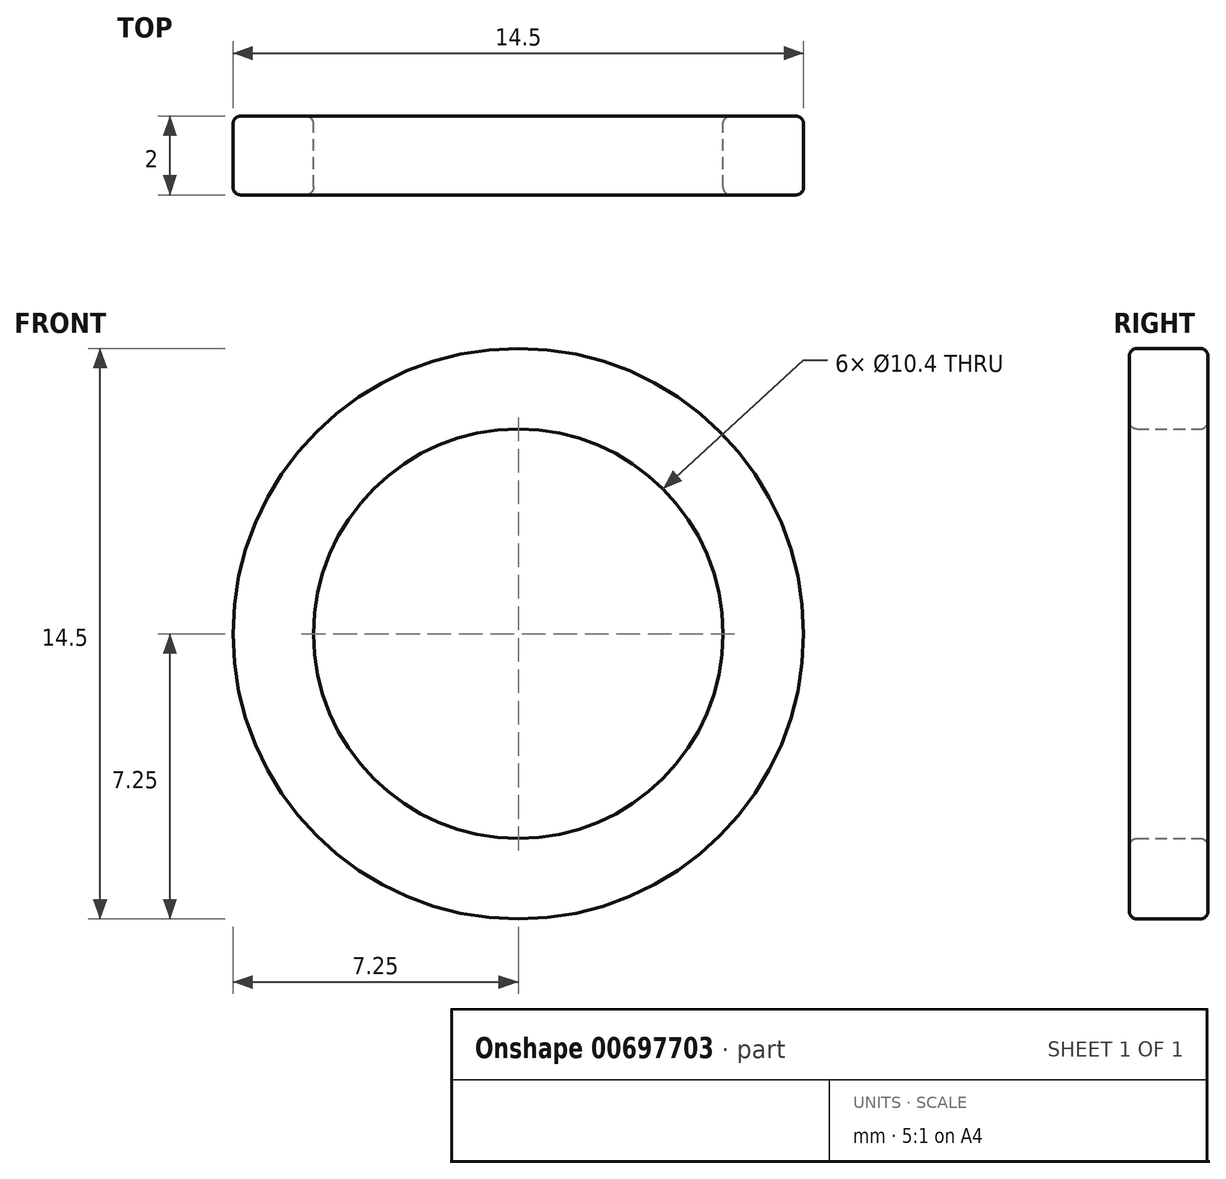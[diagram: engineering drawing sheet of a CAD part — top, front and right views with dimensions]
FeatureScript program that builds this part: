
annotation { "Feature Type Name" : "Feature", "Feature Type Description" : "" }
export const myFeature = defineFeature(function(context is Context, id is Id, definition is map)
    precondition{}
    {
        {
            var Q0;
            Q0=qCreatedBy(makeId("Front.planeOp"),FACE);
            var sketch = newSketch(context, id + "F0", { "sketchPlane" : qUnion([Q0])});
            skCircle(sketch, "E0", {"center": v(0, 0) * mm, "radius": 5.2 * mm});
            skCircle(sketch, "E1", {"center": v(0, 0) * mm, "radius": 7.25 * mm});
            skSolve(sketch);
        }
        {
            var Q0;
            Q0 = qSketchRegion(id + "F0", true);
            extrude(context, id + "F1", {"entities" : qUnion([Q0]), "depth" : 2 * mm, "offsetDistance" : 25 * mm});
        }
        {
            var Q0;
            Q0=makeQuery(id+"F1.opExtrude","CAP_FACE",FACE,{"disambiguationData":[OSD([sQuery(id+"F0.wireOp",EDGE,"E0"),sQuery(id+"F0.wireOp",EDGE,"E1")])],"isStart":false});
            var Q1;
            Q1=makeQuery(id+"F1.opExtrude","CAP_FACE",FACE,{"disambiguationData":[OSD([sQuery(id+"F0.wireOp",EDGE,"E0"),sQuery(id+"F0.wireOp",EDGE,"E1")])],"isStart":true});
            fillet(context, id + "F2", {"entities" : qUnion([Q0, Q1]), "radius" : 0.2 * mm, "tangentPropagation" : true, "allowEdgeOverflow" : false});
        }
    });
